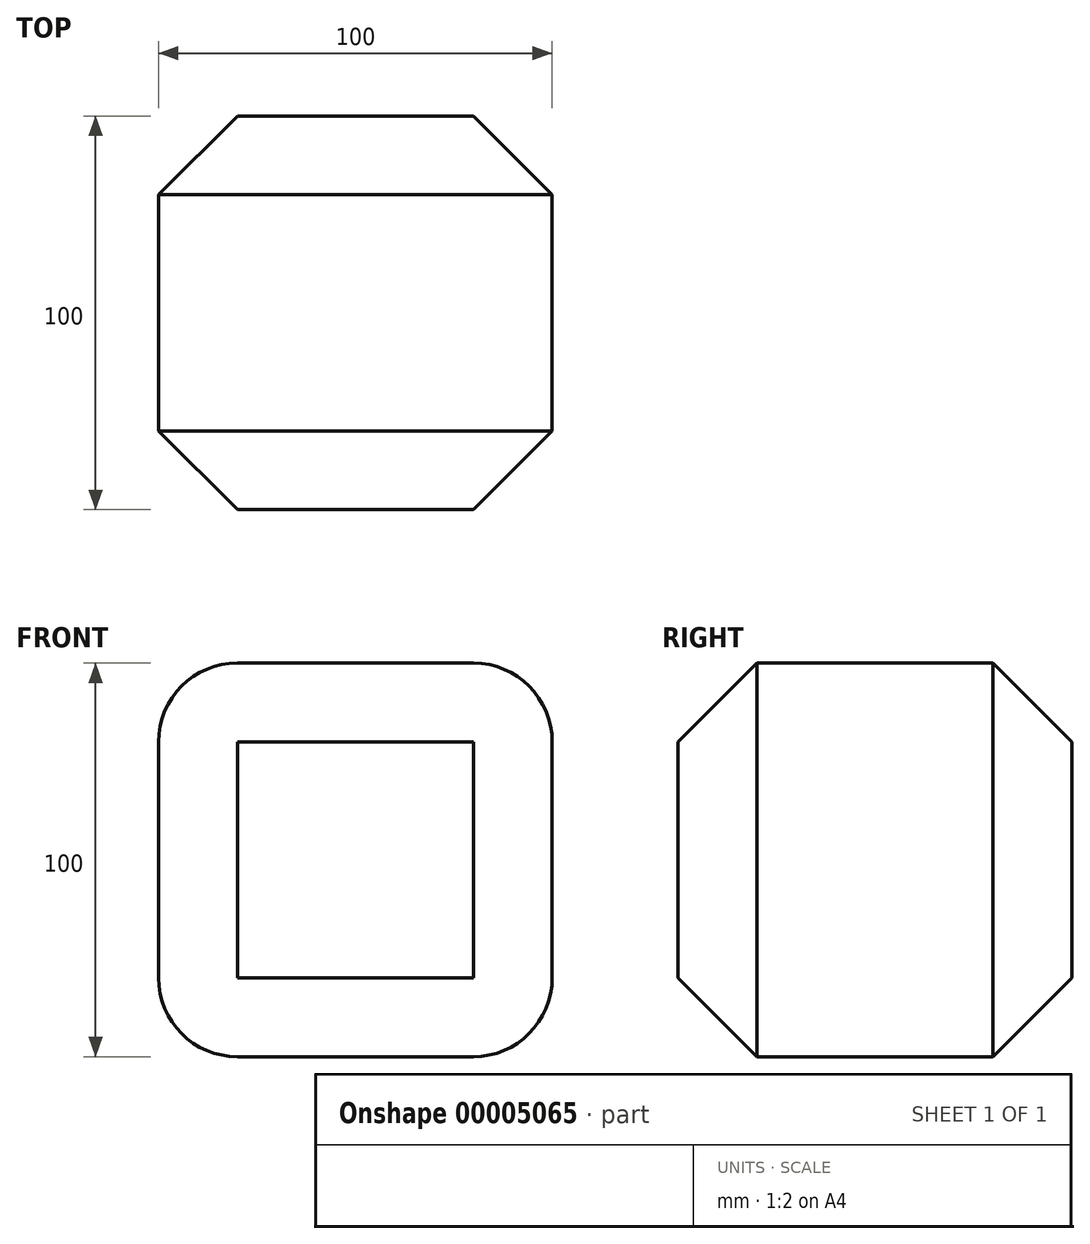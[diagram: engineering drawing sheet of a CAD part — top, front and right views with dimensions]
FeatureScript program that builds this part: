
annotation { "Feature Type Name" : "Feature", "Feature Type Description" : "" }
export const myFeature = defineFeature(function(context is Context, id is Id, definition is map)
    precondition{}
    {
        {
            var Q0;
            Q0=qCreatedBy(makeId("Front.planeOp"),FACE);
            var sketch = newSketch(context, id + "F0", { "sketchPlane" : qUnion([Q0])});
            skLineSegment(sketch, "E0.rect.bottom", {"start": v(30, -50) * mm, "end": v(-30, -50) * mm});
            skLineSegment(sketch, "E0.rect.top", {"start": v(30, 50) * mm, "end": v(-30, 50) * mm});
            skLineSegment(sketch, "E0.rect.left", {"start": v(50, -30) * mm, "end": v(50, 30) * mm});
            skLineSegment(sketch, "E0.rect.right", {"start": v(-50, -30) * mm, "end": v(-50, 30) * mm});
            skPoint(sketch, "E0.rect.middle", {"position": v(0, 0) * mm});
            skPoint(sketch, "E1.visualSharp", {"position": v(-50, 50) * mm});
            skArc(sketch, "E1.filletArc", {"start": v(-30, 50) * mm, "mid": v(-44.14, 44.14) * mm, "end": v(-50, 30) * mm});
            skPoint(sketch, "E2.visualSharp", {"position": v(50, 50) * mm});
            skArc(sketch, "E2.filletArc", {"start": v(50, 30) * mm, "mid": v(44.14, 44.14) * mm, "end": v(30, 50) * mm});
            skPoint(sketch, "E3.visualSharp", {"position": v(50, -50) * mm});
            skArc(sketch, "E3.filletArc", {"start": v(30, -50) * mm, "mid": v(44.14, -44.14) * mm, "end": v(50, -30) * mm});
            skPoint(sketch, "E4.visualSharp", {"position": v(-50, -50) * mm});
            skArc(sketch, "E4.filletArc", {"start": v(-50, -30) * mm, "mid": v(-44.14, -44.14) * mm, "end": v(-30, -50) * mm});
            skSolve(sketch);
        }
        {
            var Q0;
            Q0 = qSketchRegion(id + "F0", true);
            extrude(context, id + "F1", {"entities" : qUnion([Q0]), "depth" : 100 * mm, "symmetric" : true});
        }
        {
            var Q0;
            Q0=makeQuery(id+"F1.opExtrude","CAP_EDGE",EDGE,{"disambiguationData":[OSD([sQuery(id+"F0.wireOp",EDGE,"E1.filletArc")])],"isStart":false});
            var Q1;
            Q1=makeQuery(id+"F1.opExtrude","CAP_EDGE",EDGE,{"disambiguationData":[OSD([sQuery(id+"F0.wireOp",EDGE,"E0.rect.top")])],"isStart":false});
            var Q2;
            Q2=makeQuery(id+"F1.opExtrude","CAP_FACE",FACE,{"disambiguationData":[OSD([sQuery(id+"F0.wireOp",EDGE,"E0.rect.bottom"),sQuery(id+"F0.wireOp",EDGE,"E0.rect.top"),sQuery(id+"F0.wireOp",EDGE,"E0.rect.left"),sQuery(id+"F0.wireOp",EDGE,"E0.rect.right"),sQuery(id+"F0.wireOp",EDGE,"E1.filletArc"),sQuery(id+"F0.wireOp",EDGE,"E2.filletArc"),sQuery(id+"F0.wireOp",EDGE,"E3.filletArc"),sQuery(id+"F0.wireOp",EDGE,"E4.filletArc")])],"isStart":true});
            chamfer(context, id + "F2", {"entities" : qUnion([Q0, Q1, Q2]), "width" : 20 * mm, "tangentPropagation" : true});
        }
    });
